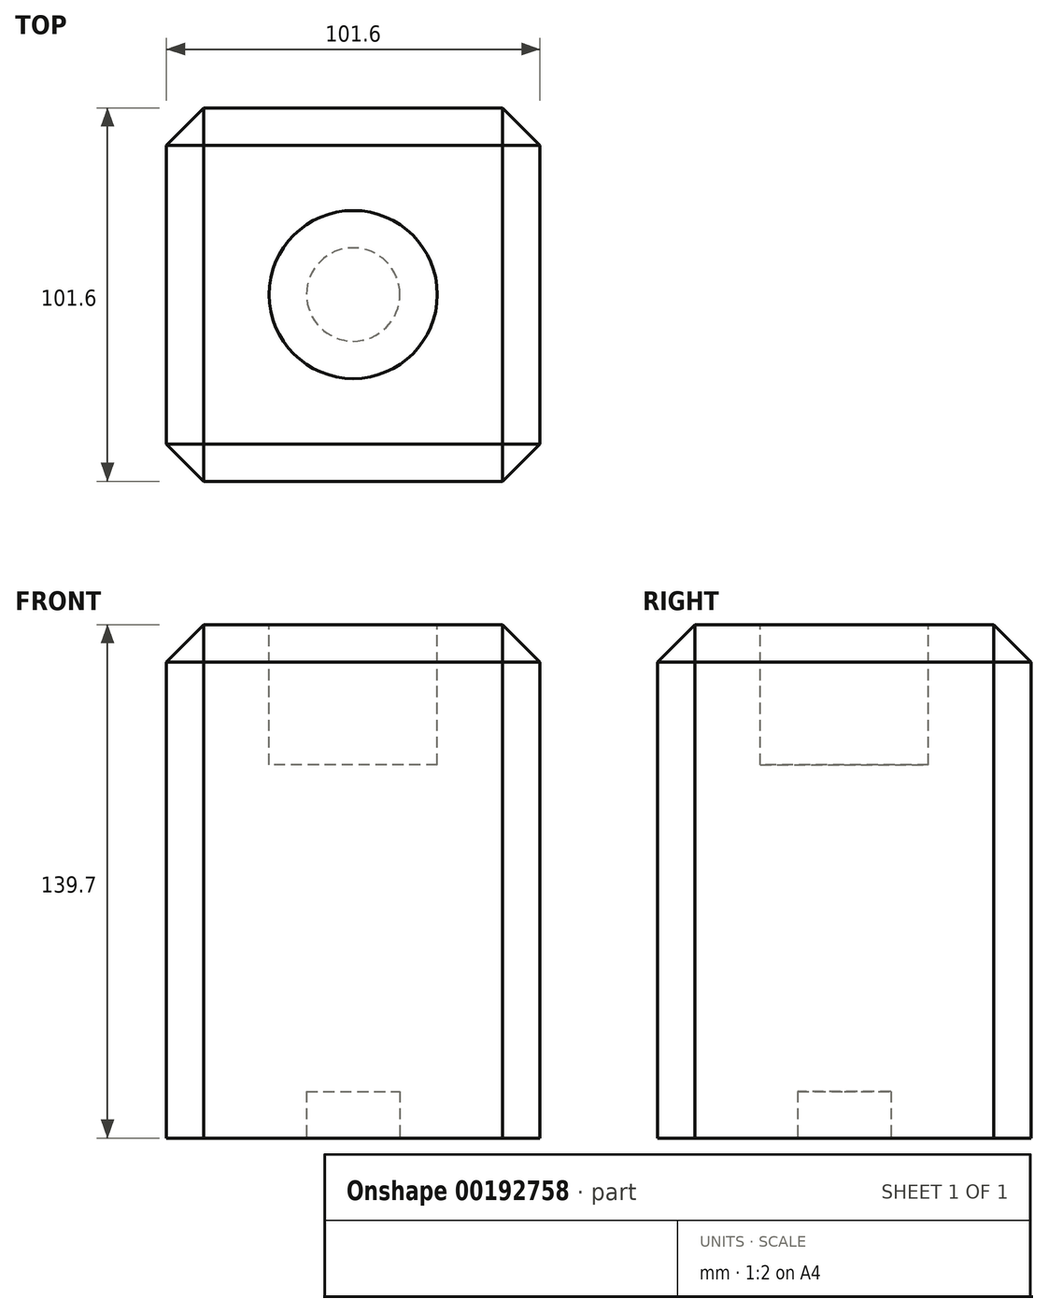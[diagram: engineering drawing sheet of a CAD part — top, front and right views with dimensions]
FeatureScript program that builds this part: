
annotation { "Feature Type Name" : "Feature", "Feature Type Description" : "" }
export const myFeature = defineFeature(function(context is Context, id is Id, definition is map)
    precondition{}
    {
        {
            var Q0;
            Q0=qCreatedBy(makeId("Top.planeOp"),FACE);
            var sketch = newSketch(context, id + "F0", { "sketchPlane" : qUnion([Q0])});
            skLineSegment(sketch, "E0.bottom", {"start": v(50.8, -50.8) * mm, "end": v(-50.8, -50.8) * mm});
            skLineSegment(sketch, "E0.top", {"start": v(50.8, 50.8) * mm, "end": v(-50.8, 50.8) * mm});
            skLineSegment(sketch, "E0.left", {"start": v(50.8, -50.8) * mm, "end": v(50.8, 50.8) * mm});
            skLineSegment(sketch, "E0.right", {"start": v(-50.8, -50.8) * mm, "end": v(-50.8, 50.8) * mm});
            skPoint(sketch, "E0.middle", {"position": v(0, 0) * mm});
            skSolve(sketch);
        }
        {
            var Q0;
            Q0=makeQuery(id+"F0.imprint","IMPRINT",FACE,{"disambiguationData":[TD([[makeQuery(id+"F0.imprint","IMPRINT",EDGE,{"derivedFrom":sQuery(id+"F0.wireOp",EDGE,"E0.bottom")}),-1.0]])]});
            extrude(context, id + "F1", {"entities" : qUnion([Q0]), "depth" : 139.7 * mm});
        }
        {
            var Q0;
            Q0=makeQuery(id+"F1.opExtrude","CAP_EDGE",EDGE,{"disambiguationData":[OSD([sQuery(id+"F0.wireOp",EDGE,"E0.bottom")])],"isStart":false});
            var Q1;
            Q1=makeQuery(id+"F1.opExtrude","CAP_EDGE",EDGE,{"disambiguationData":[OSD([sQuery(id+"F0.wireOp",EDGE,"E0.right")])],"isStart":false});
            var Q2;
            Q2=makeQuery(id+"F1.opExtrude","CAP_EDGE",EDGE,{"disambiguationData":[OSD([sQuery(id+"F0.wireOp",EDGE,"E0.left")])],"isStart":false});
            var Q3;
            Q3=makeQuery(id+"F1.opExtrude","CAP_EDGE",EDGE,{"disambiguationData":[OSD([sQuery(id+"F0.wireOp",EDGE,"E0.top")])],"isStart":false});
            var Q4;
            Q4=makeQuery(id+"F1.opExtrude","SWEPT_EDGE",EDGE,{"disambiguationData":[OSD([sQuery(id+"F0.wireOp",EDGE,"E0.top"),sQuery(id+"F0.wireOp",EDGE,"E0.right")])]});
            var Q5;
            Q5=makeQuery(id+"F1.opExtrude","SWEPT_EDGE",EDGE,{"disambiguationData":[OSD([sQuery(id+"F0.wireOp",EDGE,"E0.top"),sQuery(id+"F0.wireOp",EDGE,"E0.left")])]});
            var Q6;
            Q6=makeQuery(id+"F1.opExtrude","SWEPT_EDGE",EDGE,{"disambiguationData":[OSD([sQuery(id+"F0.wireOp",EDGE,"E0.bottom"),sQuery(id+"F0.wireOp",EDGE,"E0.left")])]});
            var Q7;
            Q7=makeQuery(id+"F1.opExtrude","SWEPT_EDGE",EDGE,{"disambiguationData":[OSD([sQuery(id+"F0.wireOp",EDGE,"E0.bottom"),sQuery(id+"F0.wireOp",EDGE,"E0.right")])]});
            chamfer(context, id + "F2", {"entities" : qUnion([Q0, Q1, Q2, Q3, Q4, Q5, Q6, Q7]), "width" : 10.16 * mm, "tangentPropagation" : true});
        }
        {
            var Q0;
            Q0=makeQuery(id+"F1.opExtrude","CAP_FACE",FACE,{"disambiguationData":[OSD([sQuery(id+"F0.wireOp",EDGE,"E0.bottom"),sQuery(id+"F0.wireOp",EDGE,"E0.top"),sQuery(id+"F0.wireOp",EDGE,"E0.left"),sQuery(id+"F0.wireOp",EDGE,"E0.right")])],"isStart":false});
            var sketch = newSketch(context, id + "F3", { "sketchPlane" : qUnion([Q0])});
            skCircle(sketch, "E1", {"center": v(0, 0) * mm, "radius": 22.86 * mm});
            skSolve(sketch);
        }
        {
            var Q0;
            Q0=makeQuery(id+"F3.imprint","IMPRINT",FACE,{"disambiguationData":[TD([[makeQuery(id+"F3.imprint","IMPRINT",EDGE,{"derivedFrom":sQuery(id+"F3.wireOp",EDGE,"E1")}),1.0]])]});
            extrude(context, id + "F4", {"entities" : qUnion([Q0]), "operationType" : NewBodyOperationType.REMOVE, "oppositeDirection" : true, "depth" : 38.1 * mm});
        }
        {
            var Q0;
            Q0=makeQuery(id+"F1.opExtrude","CAP_FACE",FACE,{"disambiguationData":[OSD([sQuery(id+"F0.wireOp",EDGE,"E0.bottom"),sQuery(id+"F0.wireOp",EDGE,"E0.top"),sQuery(id+"F0.wireOp",EDGE,"E0.left"),sQuery(id+"F0.wireOp",EDGE,"E0.right")])],"isStart":true});
            var sketch = newSketch(context, id + "F5", { "sketchPlane" : qUnion([Q0])});
            skCircle(sketch, "E2", {"center": v(0, 0) * mm, "radius": 12.7 * mm});
            skSolve(sketch);
        }
        {
            var Q0;
            Q0=makeQuery(id+"F5.imprint","IMPRINT",FACE,{"disambiguationData":[TD([[makeQuery(id+"F5.imprint","IMPRINT",EDGE,{"derivedFrom":sQuery(id+"F5.wireOp",EDGE,"E2")}),1.0]])]});
            extrude(context, id + "F6", {"entities" : qUnion([Q0]), "operationType" : NewBodyOperationType.REMOVE, "oppositeDirection" : true, "depth" : 12.7 * mm});
        }
    });
